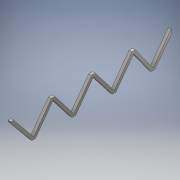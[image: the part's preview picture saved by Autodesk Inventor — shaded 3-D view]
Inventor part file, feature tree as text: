
AUTODESK INVENTOR PART (.ipt)
format: ipt  version: 2016 (Build 200138000, 138)  size: 158,208 bytes
history: native  units: mm
features: extrude x1, sketch x1
ambient origin geometry x8: Origin, YZ Plane, XZ Plane, XY Plane, X Axis, Y Axis, Z Axis, Center Point
bodies: Body1 (feature_tree)
feature tree (2):
  extrude  "Extrusion2"  Depth=1300.0mm
  sketch  "Sketch1"  dims[d0=972.5mm d1=1300.0mm d5=972.5mm d6=140.0mm d7=1965.0mm d8=140.0mm d9=140.0mm d10=1965.0mm d11=140.0mm d12=140.0mm d13=1965.0mm d14=140.0mm d24=35.0mm d27=140.0mm d28=140.0mm d29=0.0mm d32=140.0mm]
